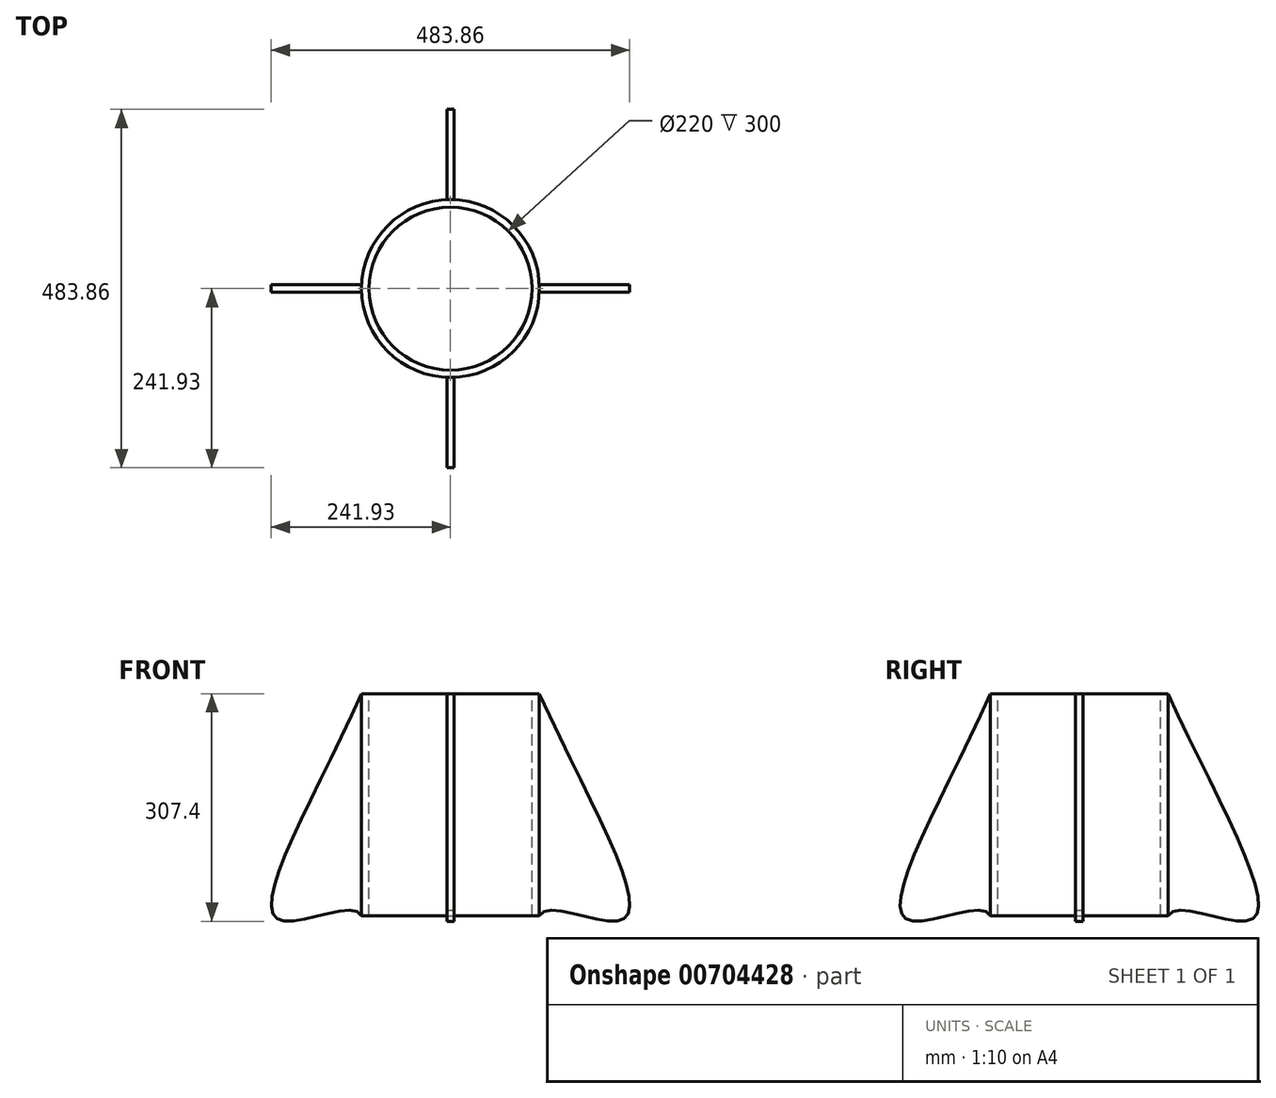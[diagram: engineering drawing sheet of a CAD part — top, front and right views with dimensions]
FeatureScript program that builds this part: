
annotation { "Feature Type Name" : "Feature", "Feature Type Description" : "" }
export const myFeature = defineFeature(function(context is Context, id is Id, definition is map)
    precondition{}
    {
        {
            var Q0;
            Q0=qCreatedBy(makeId("Front.planeOp"),FACE);
            var sketch = newSketch(context, id + "F0", { "sketchPlane" : qUnion([Q0])});
            skLineSegment(sketch, "E0", {"start": v(-110, 150.08) * mm, "end": v(-110, -149.92) * mm});
            skLineSegment(sketch, "E1", {"start": v(0, 171.72) * mm, "end": v(0, -162.35) * mm, "construction": true});
            skLineSegment(sketch, "E2", {"start": v(-120, 150.08) * mm, "end": v(-120, -149.92) * mm});
            skLineSegment(sketch, "E3", {"start": v(-120, 150.08) * mm, "end": v(-110, 150.08) * mm});
            skLineSegment(sketch, "E4", {"start": v(-120, -149.92) * mm, "end": v(-110, -149.92) * mm});
            skFitSpline(sketch, "E5", {"points": [v(-120, 150.08) * mm, v(-229.59, -156.1) * mm, v(-120, -149.92) * mm], "startDerivative": vector(-302.56, -675.29) * mm, "endDerivative": vector(82.25, -186.84) * mm});
            skSolve(sketch);
        }
        {
            var Q0;
            Q0=makeQuery(id+"F0.imprint","IMPRINT",FACE,{"disambiguationData":[TD([[makeQuery(id+"F0.imprint","IMPRINT",EDGE,{"derivedFrom":sQuery(id+"F0.wireOp",EDGE,"E0")}),-1.0]])]});
            var Q1;
            Q1=sQuery(id+"F0.wireOp",EDGE,"E1");
            revolve(context, id + "F1", {"surfaceOperationType" : NewSurfaceOperationType.NEW, "entities" : qUnion([Q0]), "axis" : qUnion([Q1]), "revolveType" : RevolveType.FULL});
        }
        {
            var Q0;
            Q0=makeQuery(id+"F0.imprint","IMPRINT",FACE,{"disambiguationData":[TD([[makeQuery(id+"F0.imprint","IMPRINT",EDGE,{"derivedFrom":sQuery(id+"F0.wireOp",EDGE,"E2")}),-1.0]])]});
            extrude(context, id + "F2", {"entities" : qUnion([Q0]), "operationType" : NewBodyOperationType.ADD, "endBound" : BoundingType.SYMMETRIC, "depth" : 10 * mm, "offsetDistance" : 25 * mm});
        }
        {
            var Q0;
            Q0=makeQuery(id+"F2.opExtrude","SWEPT_BODY",BODY,{"disambiguationData":[OSD([sQuery(id+"F0.wireOp",EDGE,"E2"),sQuery(id+"F0.wireOp",EDGE,"E5")])]});
            var Q1;
            Q1=sQuery(id+"F0.wireOp",EDGE,"E1");
            circularPattern(context, id + "F3", {"entities" : qUnion([Q0]), "axis" : qUnion([Q1]), "angle" : 360 * degree, "instanceCount" : 4, "equalSpace" : true});
        }
    });
